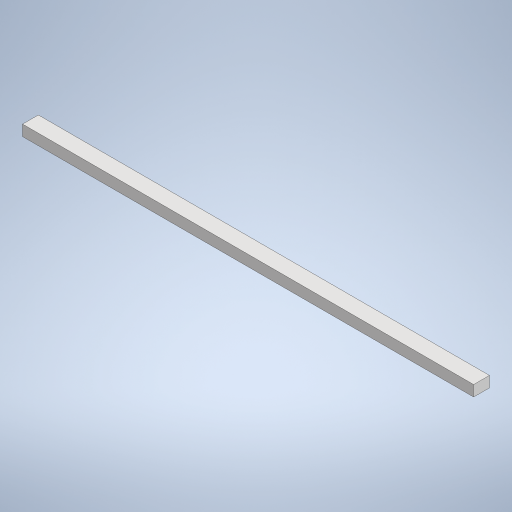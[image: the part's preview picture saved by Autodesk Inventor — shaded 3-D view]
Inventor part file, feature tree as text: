
AUTODESK INVENTOR PART (.ipt)
format: ipt  version: 2024 (Build 280153000, 153)  size: 237,568 bytes
history: native  units: mm
features: extrude x1, sketch x1
ambient origin geometry x8: Origin, YZ Plane, XZ Plane, XY Plane, X Axis, Y Axis, Z Axis, Center Point
bodies: Solid1 (feature_tree)
feature tree (2):
  extrude  "Extrusion1"  Depth=7.0mm
  sketch  "Sketch1"  dims[d0=4.8mm d1=7.0mm d2=200.0mm d3=0.0mm]
